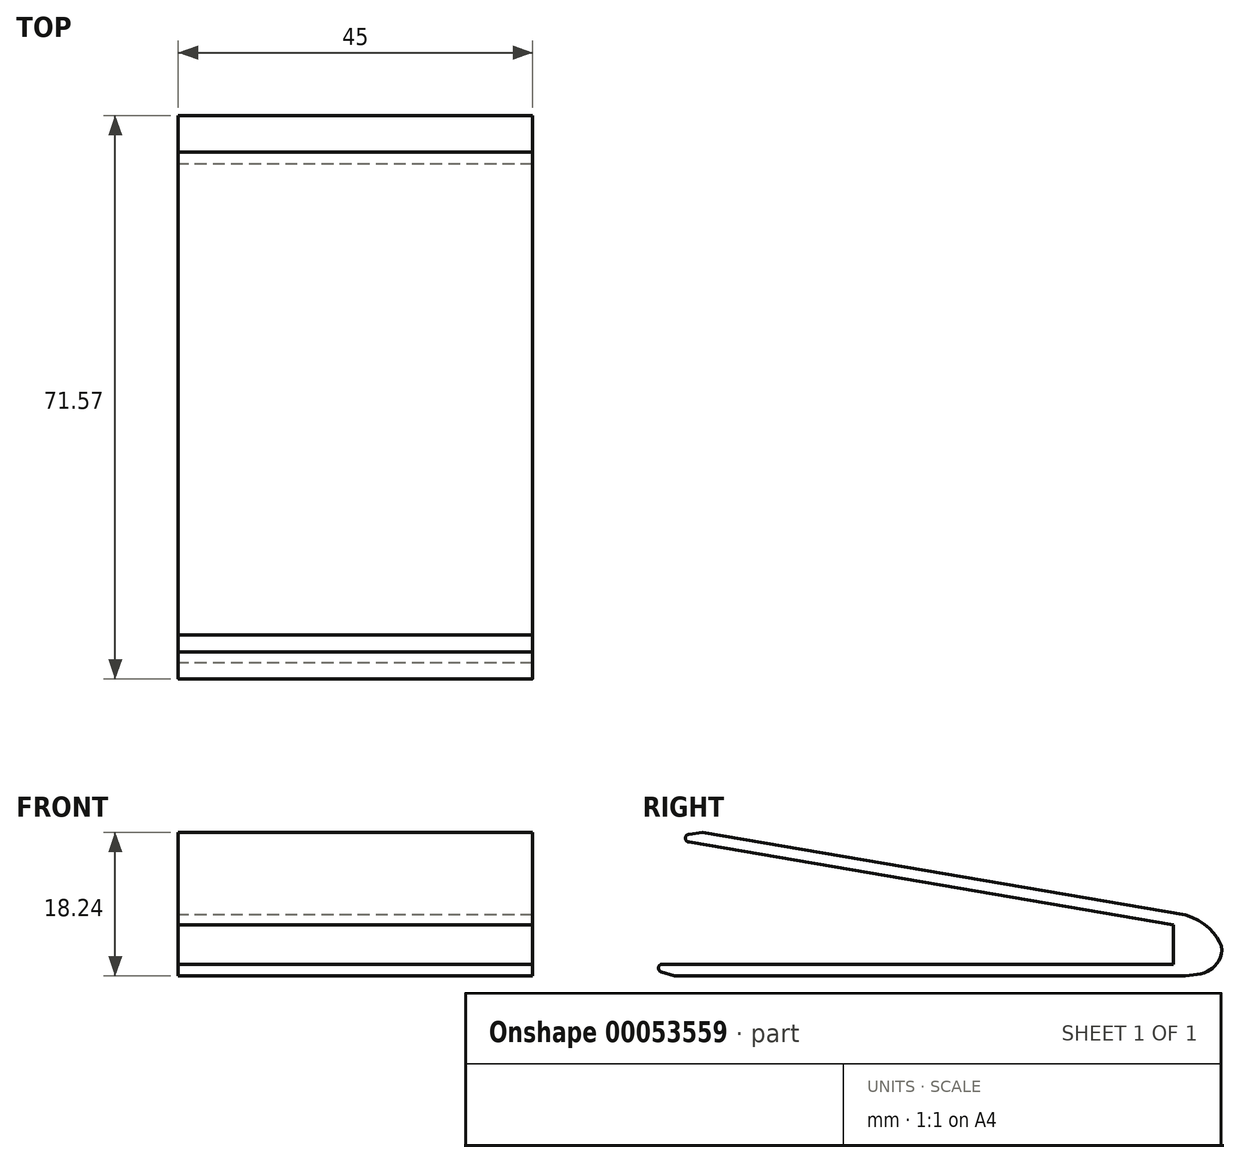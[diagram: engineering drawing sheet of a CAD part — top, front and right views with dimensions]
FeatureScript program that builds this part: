
annotation { "Feature Type Name" : "Feature", "Feature Type Description" : "" }
export const myFeature = defineFeature(function(context is Context, id is Id, definition is map)
    precondition{}
    {
        {
            var Q0;
            Q0=qCreatedBy(makeId("Right.planeOp"),FACE);
            var sketch = newSketch(context, id + "F0", { "sketchPlane" : qUnion([Q0])});
            skPoint(sketch, "E0", {"position": v(0, 5) * mm});
            skPoint(sketch, "E1", {"position": v(-13, 0) * mm});
            skLineSegment(sketch, "E2", {"start": v(0, 5) * mm, "end": v(0, 0) * mm});
            skLineSegment(sketch, "E3", {"start": v(0, 0) * mm, "end": v(-13, 0) * mm});
            skLineSegment(sketch, "E4", {"start": v(-13, 0) * mm, "end": v(-60, 0) * mm});
            skPoint(sketch, "E5", {"position": v(-41, 12) * mm});
            skLineSegment(sketch, "E6", {"start": v(0, 5) * mm, "end": v(-41, 12) * mm});
            skLineSegment(sketch, "E7", {"start": v(-41, 12) * mm, "end": v(-60, 15.24) * mm});
            skLineSegment(sketch, "E8.0", {"start": v(-15.94, -1.5) * mm, "end": v(-63.41, -1.5) * mm});
            skLineSegment(sketch, "E8.1", {"start": v(-40.75, 13.48) * mm, "end": v(-59.84, 16.74) * mm});
            skLineSegment(sketch, "E8.2", {"start": v(1.5, 6.27) * mm, "end": v(-40.75, 13.48) * mm});
            skLineSegment(sketch, "E8.3", {"start": v(1.5, 6.27) * mm, "end": v(1.5, -1.5) * mm, "construction": true});
            skLineSegment(sketch, "E8.4", {"start": v(1.5, -1.5) * mm, "end": v(-15.94, -1.5) * mm});
            skLineSegment(sketch, "E9", {"start": v(-63.41, -1.5) * mm, "end": v(-68.18, 0) * mm});
            skLineSegment(sketch, "E10", {"start": v(-68.18, 0) * mm, "end": v(-60, 0) * mm});
            skLineSegment(sketch, "E11", {"start": v(-60, 15.24) * mm, "end": v(-64.79, 16.06) * mm});
            skLineSegment(sketch, "E12", {"start": v(-59.84, 16.74) * mm, "end": v(-64.79, 16.06) * mm});
            skFitSpline(sketch, "E13", {"points": [v(1.5, 6.27) * mm, v(6.1, 2.16) * mm, v(5.47, 0) * mm, v(4.03, -1.04) * mm, v(1.5, -1.5) * mm], "startDerivative": vector(20.6, -6.4) * mm, "endDerivative": vector(-11.66, -1.2) * mm});
            skSolve(sketch);
        }
        {
            var Q0;
            Q0=qSketchRegion(id+"F0",true);
            extrude(context, id + "F1", {"entities" : qUnion([Q0]), "depth" : 40 * mm, "symmetric" : true});
        }
        {
            var Q0;
            Q0 = qSketchRegion(id + "F0", true);
            extrude(context, id + "F2", {"entities" : qUnion([Q0]), "operationType" : NewBodyOperationType.ADD, "depth" : 25 * mm});
        }
        {
            var Q0;
            {var subQ0=sQuery(id+"F0.wireOp",EDGE,"E12");var subQ1=sQuery(id+"F0.wireOp",EDGE,"E11");Q0=makeQuery(id+"F2.boolean.opBoolean","MERGE",EDGE,{"derivedFrom":[makeQuery(id+"F1.opExtrude","SWEPT_EDGE",EDGE,{"disambiguationData":[OSD([subQ1,subQ0])]}),makeQuery(id+"F2.opExtrude","SWEPT_EDGE",EDGE,{"disambiguationData":[OSD([subQ1,subQ0])]})]});}
            var Q1;
            {var subQ0=sQuery(id+"F0.wireOp",EDGE,"E10");var subQ1=sQuery(id+"F0.wireOp",EDGE,"E9");Q1=makeQuery(id+"F2.boolean.opBoolean","MERGE",EDGE,{"derivedFrom":[makeQuery(id+"F1.opExtrude","SWEPT_EDGE",EDGE,{"disambiguationData":[OSD([subQ1,subQ0])]}),makeQuery(id+"F2.opExtrude","SWEPT_EDGE",EDGE,{"disambiguationData":[OSD([subQ1,subQ0])]})]});}
            fillet(context, id + "F3", {"entities" : qUnion([Q0, Q1]), "radius" : .5 * mm, "tangentPropagation" : true, "allowEdgeOverflow" : false});
        }
    });
